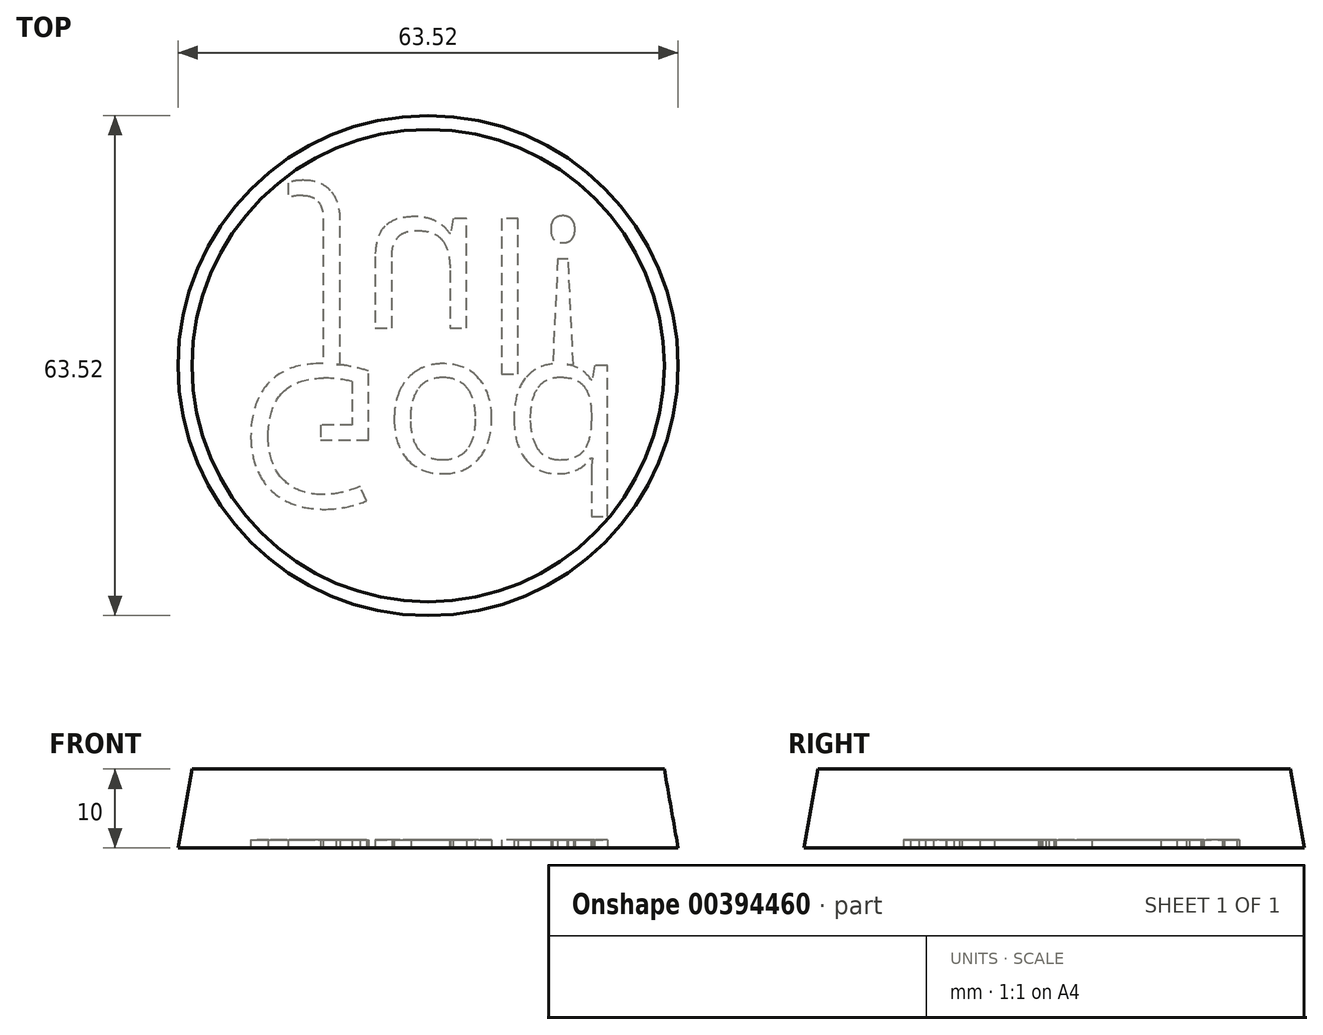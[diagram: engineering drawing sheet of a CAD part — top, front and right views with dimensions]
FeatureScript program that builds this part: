
annotation { "Feature Type Name" : "Feature", "Feature Type Description" : "" }
export const myFeature = defineFeature(function(context is Context, id is Id, definition is map)
    precondition{}
    {
        {
            var Q0;
            Q0=qCreatedBy(makeId("Top.planeOp"),FACE);
            var sketch = newSketch(context, id + "F0", { "sketchPlane" : qUnion([Q0])});
            skCircle(sketch, "E0", {"center": v(0, 0) * mm, "radius": 30 * mm});
            skSolve(sketch);
        }
        {
            var Q0;
            Q0=makeQuery(id+"F0.imprint","IMPRINT",FACE,{"disambiguationData":[TD([[makeQuery(id+"F0.imprint","IMPRINT",EDGE,{"derivedFrom":sQuery(id+"F0.wireOp",EDGE,"E0")}),1.0]])]});
            extrude(context, id + "F1", {"entities" : qUnion([Q0]), "oppositeDirection" : true, "depth" : 10 * mm, "hasDraft" : true, "draftAngle" : 10 * degree});
        }
        {
            var Q0;
            Q0=makeQuery(id+"F1.opExtrude","CAP_FACE",FACE,{"disambiguationData":[OSD([sQuery(id+"F0.wireOp",EDGE,"E0")])],"isStart":false});
            var sketch = newSketch(context, id + "F2", { "sketchPlane" : qUnion([Q0])});
            skText(sketch, "E1", { "text": "God", "fontName": "OpenSans-Regular.ttf"});
            skText(sketch, "E2", { "text": "Jul!", "fontName": "OpenSans-Regular.ttf"});
            const initialGuessF2  = {"E1": [-0.02406, 0, 1, 0, 0.01814], "E2": [-0.01573, -0.01867, 1, 0, 0.01867]};
            skSetInitialGuess(sketch, initialGuessF2);
            skSolve(sketch);
        }
        {
            var Q0;
            Q0 = qSketchRegion(id + "F2", true);
            extrude(context, id + "F3", {"entities" : qUnion([Q0]), "operationType" : NewBodyOperationType.REMOVE, "oppositeDirection" : true, "depth" : 1 * mm});
        }
    });
